# Revit family: Broan®_AI_Series™-Heat_Recovery_Ventilator_(HRV)-Top_Port
name_source: partatom
category: Mechanical Equipment
units: mm (PartAtom-declared; Revit-internal decimal feet)

## family parameters
Always vertical = No
Classification = None
Cut with Voids When Loaded = No
Part Type = Normal
Room Calculation Point = No
Round Connector Dimension = Use Diameter
Shared = No
Work Plane-Based = Yes

## types (5) — shared parameters
Default Elevation = 0.00"
Frequency = 60 Hz
Height = 21.58"
Length = 16.14"
Manufacturer = Broan
Number of Poles = 1
Operating Weight = 35.00 lb
Phase = 1
Product Documentation Link = https://www.broan-nutone.com
Product Page URL = https://www.broan-nutone.com
URL = https://www.broan-nutone.com
Voltage = 120 V
Width = 21.07"
c Back Clearance = 0.00"
c Front Clearance = 8.00"
c Height = 19.13"
c Left Clearance = 0.00"
c MC width = 12.14"
c Offset vent side = 3.79"
c Right Clrearence = 0.00"
c Vent Height = 2.45"
c Width = 18.75"
c Width MC = 2.32"
zero-valued in all types: Power Factor

## per-type parameters (varying)
| type | Air Volume | Exhaust Air Connection Diameter | Fan Wattage | Model | Noise | Product Name | Requirements and Standards | Return Air Connection Diameter | Supply Air Connection Diameter | c Constraints | c Gen Diameter | c Top Clearance |
| Broan®_AI_Series™-130_CFM-Heat_Recovery_Ventilator_(HRV)-Top_Port-65%_eff | 130 CFM | 5" | 110 W | B130H65RT | 70 | Broan® AI Series™ 130 CFM Heat Recovery Ventilator (HRV) | UL 1812
CSA F326
CSA C439
Prop 65 | 5" | 5" | 2 | 5.00" | 8.00" |
| Broan®_AI_Series™-110_CFM-Heat_Recovery_Ventilator_(HRV)-Top_Port-65%_eff | 110 CFM | 5" | 90 W | B110H65RT | 66.8 | Broan® AI Series™ 110 CFM Heat Recovery Ventilator (HRV) | UL 1812
CSA F326
CSA C439
Prop 65 | 5" | 5" | 1 | 5.00" | 8.00" |
| Broan®_AI_Series™-150_CFM-Heat_Recovery_Ventilator_(HRV)-Top_Port-75%_eff | 150 CFM | 5" | 163 W | B150H75NT | 73.2 | Broan® AI Series™ 150 CFM Heat Recovery Ventilator (HRV) | UL 1812
CSA F326
CSA C439
Prop 65
ENERGY STAR® | 5" | 5" | 3 | 5.00" | 8.00" |
| Broan®_AI_Series™-160_CFM-Heat_Recovery_Ventilator_(HRV)-Top_Port-65%_eff | 160 CFM | 6" | 163 W | B160H65RT | 73.2 | Broan® AI Series™ 160 CFM Heat Recovery Ventilator (HRV) | UL 1812
CSA F326
CSA C439
Prop 65
ENERGY STAR® | 6" | 6" | 4 | 6.00" | 9.00" |
| Broan®_AI_Series™-160_CFM-Heat_Recovery_Ventilator_(HRV)-Top_Port-75%_eff | 160 CFM | 6" | 163 W | B160H75RT | 73.2 | Broan® AI Series™ 160 CFM Heat Recovery Ventilator (HRV) | UL 1812
CSA F326
CSA C439
Prop 65
ENERGY STAR® | 6" | 6" | 5 | 6.00" | 9.00" |

## geometry (parser evidence)
native form markers: Sweep x8
no freeform markers — native parametric forms only
